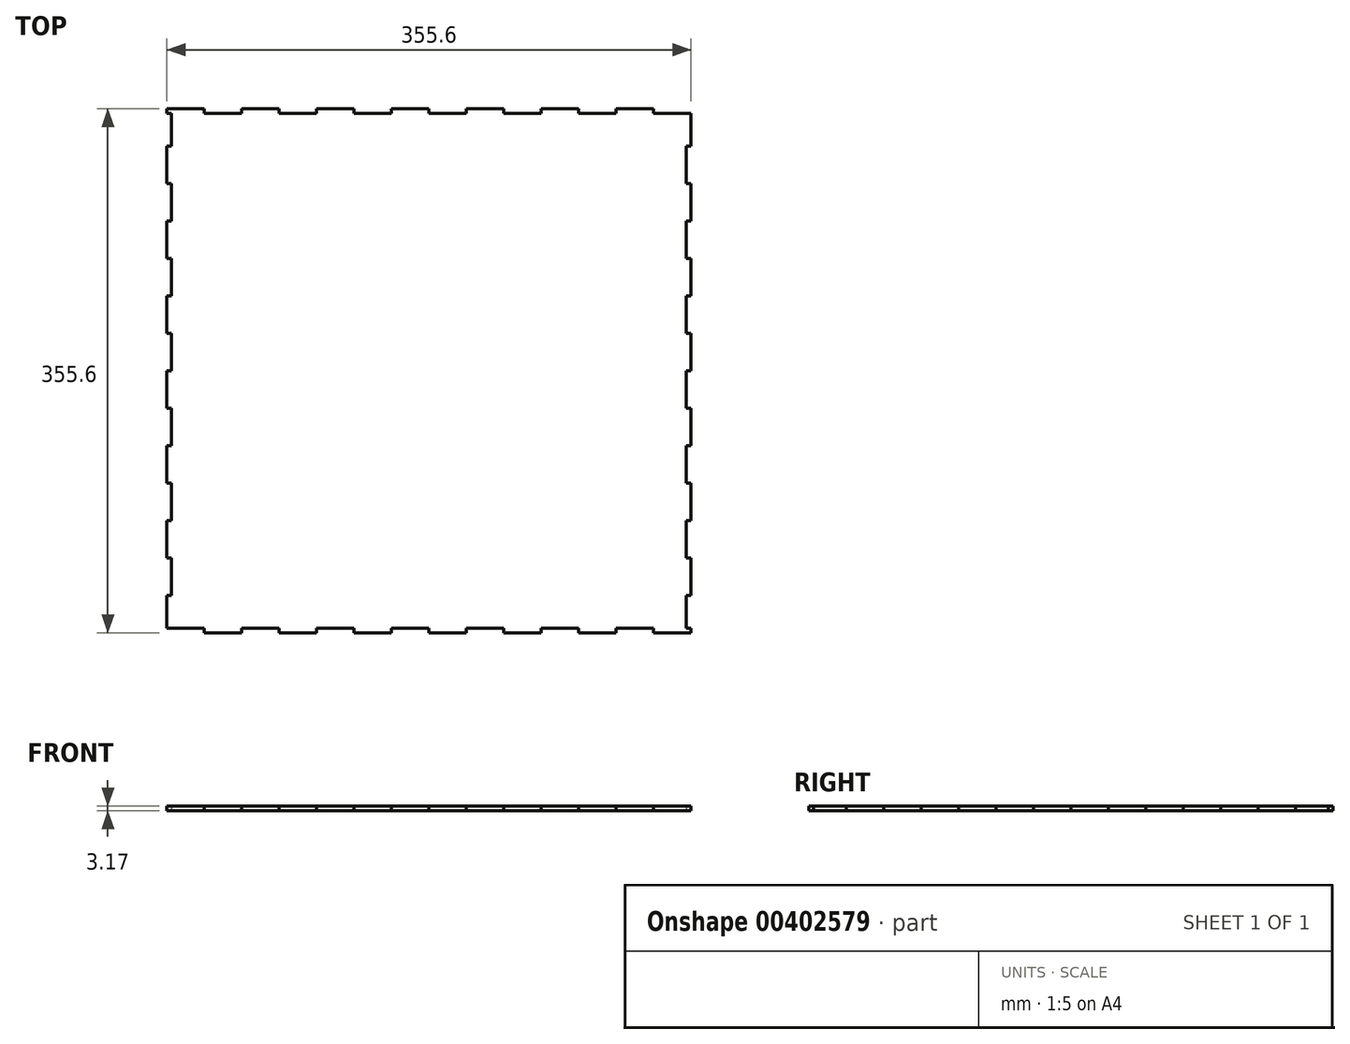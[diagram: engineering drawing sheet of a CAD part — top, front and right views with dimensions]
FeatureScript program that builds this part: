
annotation { "Feature Type Name" : "Feature", "Feature Type Description" : "" }
export const myFeature = defineFeature(function(context is Context, id is Id, definition is map)
    precondition{}
    {
        {
            var Q0;
            Q0=qCreatedBy(makeId("Top.planeOp"),FACE);
            var sketch = newSketch(context, id + "F0", { "sketchPlane" : qUnion([Q0])});
            skLineSegment(sketch, "E0.bottom", {"start": v(-177.8, 177.8) * mm, "end": v(-152.4, 177.8) * mm});
            skLineSegment(sketch, "E0.top", {"start": v(-152.4, -177.8) * mm, "end": v(-127, -177.8) * mm});
            skLineSegment(sketch, "E0.left", {"start": v(-177.8, 177.8) * mm, "end": v(-177.8, 174.62) * mm});
            skLineSegment(sketch, "E0.right", {"start": v(177.8, 174.62) * mm, "end": v(177.8, 152.4) * mm});
            skLineSegment(sketch, "E1", {"start": v(-174.62, 174.62) * mm, "end": v(-174.62, 152.4) * mm});
            skLineSegment(sketch, "E2", {"start": v(-152.4, 174.62) * mm, "end": v(-127, 174.62) * mm});
            skLineSegment(sketch, "E3", {"start": v(174.62, 152.4) * mm, "end": v(174.62, 127) * mm});
            skLineSegment(sketch, "E4", {"start": v(152.4, -174.62) * mm, "end": v(127, -174.62) * mm});
            skLineSegment(sketch, "E5", {"start": v(-152.4, 177.8) * mm, "end": v(-152.4, 174.62) * mm});
            skLineSegment(sketch, "E6", {"start": v(-174.62, 174.62) * mm, "end": v(-177.8, 174.62) * mm});
            skLineSegment(sketch, "E7", {"start": v(-127, 177.8) * mm, "end": v(-127, 174.62) * mm});
            skLineSegment(sketch, "E8", {"start": v(-101.6, 177.8) * mm, "end": v(-101.6, 174.62) * mm});
            skLineSegment(sketch, "E9", {"start": v(-76.2, 177.8) * mm, "end": v(-76.2, 174.62) * mm});
            skLineSegment(sketch, "E10", {"start": v(-50.8, 177.8) * mm, "end": v(-50.8, 174.62) * mm});
            skLineSegment(sketch, "E11", {"start": v(-25.4, 177.8) * mm, "end": v(-25.4, 174.62) * mm});
            skLineSegment(sketch, "E12", {"start": v(0, 177.8) * mm, "end": v(0, 174.62) * mm});
            skLineSegment(sketch, "E13", {"start": v(25.4, 177.8) * mm, "end": v(25.4, 174.62) * mm});
            skLineSegment(sketch, "E14", {"start": v(50.8, 177.8) * mm, "end": v(50.8, 174.62) * mm});
            skLineSegment(sketch, "E15", {"start": v(76.2, 177.8) * mm, "end": v(76.2, 174.63) * mm});
            skLineSegment(sketch, "E16", {"start": v(101.6, 177.8) * mm, "end": v(101.6, 174.63) * mm});
            skLineSegment(sketch, "E17", {"start": v(127, 177.8) * mm, "end": v(127, 174.63) * mm});
            skLineSegment(sketch, "E18", {"start": v(152.4, 177.8) * mm, "end": v(152.4, 174.63) * mm});
            skLineSegment(sketch, "E19.trimOffspring", {"start": v(-127, 177.8) * mm, "end": v(-101.6, 177.8) * mm});
            skLineSegment(sketch, "E20.trimOffspring", {"start": v(-101.6, 174.62) * mm, "end": v(-76.2, 174.62) * mm});
            skLineSegment(sketch, "E21.trimOffspring", {"start": v(-76.2, 177.8) * mm, "end": v(-50.8, 177.8) * mm});
            skLineSegment(sketch, "E22.trimOffspring", {"start": v(-50.8, 174.62) * mm, "end": v(-25.4, 174.62) * mm});
            skLineSegment(sketch, "E23.trimOffspring", {"start": v(-25.4, 177.8) * mm, "end": v(0, 177.8) * mm});
            skLineSegment(sketch, "E24.trimOffspring", {"start": v(0, 174.62) * mm, "end": v(25.4, 174.62) * mm});
            skLineSegment(sketch, "E25.trimOffspring", {"start": v(25.4, 177.8) * mm, "end": v(50.8, 177.8) * mm});
            skLineSegment(sketch, "E26.trimOffspring", {"start": v(50.8, 174.62) * mm, "end": v(76.2, 174.62) * mm});
            skLineSegment(sketch, "E27.trimOffspring", {"start": v(76.2, 177.8) * mm, "end": v(101.6, 177.8) * mm});
            skLineSegment(sketch, "E28.trimOffspring", {"start": v(101.6, 174.62) * mm, "end": v(127, 174.62) * mm});
            skLineSegment(sketch, "E29.trimOffspring", {"start": v(127, 177.8) * mm, "end": v(152.4, 177.8) * mm});
            skLineSegment(sketch, "E30.trimOffspring", {"start": v(152.4, 174.62) * mm, "end": v(174.63, 174.62) * mm});
            skLineSegment(sketch, "E31", {"start": v(174.62, 174.62) * mm, "end": v(177.8, 174.62) * mm});
            skLineSegment(sketch, "E32", {"start": v(-174.62, -174.62) * mm, "end": v(-177.8, -174.62) * mm});
            skLineSegment(sketch, "E33", {"start": v(152.4, -174.62) * mm, "end": v(152.4, -177.8) * mm});
            skLineSegment(sketch, "E34", {"start": v(127, -174.62) * mm, "end": v(127, -177.8) * mm});
            skLineSegment(sketch, "E35", {"start": v(101.6, -174.62) * mm, "end": v(101.6, -177.8) * mm});
            skLineSegment(sketch, "E36", {"start": v(76.2, -174.62) * mm, "end": v(76.2, -177.8) * mm});
            skLineSegment(sketch, "E37", {"start": v(50.8, -174.62) * mm, "end": v(50.8, -177.8) * mm});
            skLineSegment(sketch, "E38", {"start": v(25.4, -174.62) * mm, "end": v(25.4, -177.8) * mm});
            skPoint(sketch, "E39.endSnap0", {"position": v(0, -177.8) * mm});
            skLineSegment(sketch, "E40", {"start": v(-25.4, -174.62) * mm, "end": v(-25.4, -177.8) * mm});
            skLineSegment(sketch, "E41", {"start": v(-50.8, -174.62) * mm, "end": v(-50.8, -177.8) * mm});
            skLineSegment(sketch, "E42", {"start": v(-76.2, -174.62) * mm, "end": v(-76.2, -177.8) * mm});
            skLineSegment(sketch, "E43", {"start": v(-101.6, -174.62) * mm, "end": v(-101.6, -177.8) * mm});
            skLineSegment(sketch, "E44", {"start": v(-127, -174.62) * mm, "end": v(-127, -177.8) * mm});
            skLineSegment(sketch, "E45", {"start": v(-152.4, -174.62) * mm, "end": v(-152.4, -177.8) * mm});
            skPoint(sketch, "E46.orphan", {"position": v(-177.8, -177.8) * mm});
            skLineSegment(sketch, "E47.trimOffspring", {"start": v(-101.6, -177.8) * mm, "end": v(-76.2, -177.8) * mm});
            skLineSegment(sketch, "E48.trimOffspring", {"start": v(-101.6, -174.62) * mm, "end": v(-127, -174.62) * mm});
            skLineSegment(sketch, "E49.trimOffspring", {"start": v(-152.4, -174.62) * mm, "end": v(-174.62, -174.62) * mm});
            skLineSegment(sketch, "E50.trimOffspring", {"start": v(-50.8, -177.8) * mm, "end": v(-25.4, -177.8) * mm});
            skLineSegment(sketch, "E51.trimOffspring", {"start": v(-50.8, -174.62) * mm, "end": v(-76.2, -174.62) * mm});
            skLineSegment(sketch, "E52.trimOffspring", {"start": v(0, -177.8) * mm, "end": v(25.4, -177.8) * mm});
            skLineSegment(sketch, "E53", {"start": v(0, -174.62) * mm, "end": v(0, -177.8) * mm});
            skLineSegment(sketch, "E54.trimOffspring", {"start": v(0, -174.62) * mm, "end": v(-25.4, -174.62) * mm});
            skLineSegment(sketch, "E55.trimOffspring", {"start": v(50.8, -177.8) * mm, "end": v(76.2, -177.8) * mm});
            skLineSegment(sketch, "E56.trimOffspring", {"start": v(50.8, -174.62) * mm, "end": v(25.4, -174.62) * mm});
            skLineSegment(sketch, "E57.trimOffspring", {"start": v(101.6, -177.8) * mm, "end": v(127, -177.8) * mm});
            skLineSegment(sketch, "E58.trimOffspring", {"start": v(101.6, -174.62) * mm, "end": v(76.2, -174.62) * mm});
            skLineSegment(sketch, "E59.trimOffspring", {"start": v(152.4, -177.8) * mm, "end": v(177.8, -177.8) * mm});
            skLineSegment(sketch, "E60", {"start": v(174.62, -174.62) * mm, "end": v(177.8, -174.62) * mm});
            skLineSegment(sketch, "E61", {"start": v(174.62, 152.4) * mm, "end": v(177.8, 152.4) * mm});
            skLineSegment(sketch, "E62", {"start": v(174.62, 127) * mm, "end": v(177.8, 127) * mm});
            skLineSegment(sketch, "E63", {"start": v(174.62, 101.6) * mm, "end": v(177.8, 101.6) * mm});
            skLineSegment(sketch, "E64", {"start": v(174.62, 76.2) * mm, "end": v(177.8, 76.2) * mm});
            skLineSegment(sketch, "E65", {"start": v(174.62, 50.8) * mm, "end": v(177.8, 50.8) * mm});
            skLineSegment(sketch, "E66", {"start": v(174.62, 25.4) * mm, "end": v(177.8, 25.4) * mm});
            skLineSegment(sketch, "E67", {"start": v(174.62, 0) * mm, "end": v(177.8, 0) * mm});
            skLineSegment(sketch, "E68", {"start": v(174.62, -25.4) * mm, "end": v(177.8, -25.4) * mm});
            skLineSegment(sketch, "E69", {"start": v(174.62, -50.8) * mm, "end": v(177.8, -50.8) * mm});
            skLineSegment(sketch, "E70", {"start": v(174.62, -76.2) * mm, "end": v(177.8, -76.2) * mm});
            skLineSegment(sketch, "E71", {"start": v(174.62, -101.6) * mm, "end": v(177.8, -101.6) * mm});
            skLineSegment(sketch, "E72", {"start": v(174.62, -127) * mm, "end": v(177.8, -127) * mm});
            skLineSegment(sketch, "E73", {"start": v(174.62, -152.4) * mm, "end": v(177.8, -152.4) * mm});
            skLineSegment(sketch, "E74.trimOffspring", {"start": v(177.8, -174.62) * mm, "end": v(177.8, -177.8) * mm});
            skLineSegment(sketch, "E75.trimOffspring", {"start": v(174.62, -152.4) * mm, "end": v(174.62, -174.62) * mm});
            skLineSegment(sketch, "E76.trimOffspring", {"start": v(177.8, -127) * mm, "end": v(177.8, -152.4) * mm});
            skLineSegment(sketch, "E77.trimOffspring", {"start": v(174.62, -101.6) * mm, "end": v(174.62, -127) * mm});
            skLineSegment(sketch, "E78.trimOffspring", {"start": v(177.8, -76.2) * mm, "end": v(177.8, -101.6) * mm});
            skLineSegment(sketch, "E79.trimOffspring", {"start": v(174.62, -50.8) * mm, "end": v(174.62, -76.2) * mm});
            skLineSegment(sketch, "E80.trimOffspring", {"start": v(177.8, -25.4) * mm, "end": v(177.8, -50.8) * mm});
            skLineSegment(sketch, "E81.trimOffspring", {"start": v(174.62, 0) * mm, "end": v(174.62, -25.4) * mm});
            skLineSegment(sketch, "E82.trimOffspring", {"start": v(177.8, 25.4) * mm, "end": v(177.8, 0) * mm});
            skLineSegment(sketch, "E83.trimOffspring", {"start": v(174.62, 50.8) * mm, "end": v(174.62, 25.4) * mm});
            skLineSegment(sketch, "E84.trimOffspring", {"start": v(177.8, 76.2) * mm, "end": v(177.8, 50.8) * mm});
            skLineSegment(sketch, "E85.trimOffspring", {"start": v(174.62, 101.6) * mm, "end": v(174.62, 76.2) * mm});
            skLineSegment(sketch, "E86.trimOffspring", {"start": v(177.8, 127) * mm, "end": v(177.8, 101.6) * mm});
            skLineSegment(sketch, "E87", {"start": v(-177.8, 152.4) * mm, "end": v(-174.63, 152.4) * mm});
            skLineSegment(sketch, "E88", {"start": v(-177.8, 127) * mm, "end": v(-174.63, 127) * mm});
            skLineSegment(sketch, "E89", {"start": v(-177.8, 101.6) * mm, "end": v(-174.63, 101.6) * mm});
            skLineSegment(sketch, "E90", {"start": v(-177.8, 76.2) * mm, "end": v(-174.63, 76.2) * mm});
            skLineSegment(sketch, "E91", {"start": v(-177.8, 50.8) * mm, "end": v(-174.63, 50.8) * mm});
            skLineSegment(sketch, "E92", {"start": v(-177.8, 25.4) * mm, "end": v(-174.63, 25.4) * mm});
            skLineSegment(sketch, "E93", {"start": v(-177.8, 0) * mm, "end": v(-174.63, 0) * mm});
            skLineSegment(sketch, "E94", {"start": v(-177.8, -25.4) * mm, "end": v(-174.63, -25.4) * mm});
            skLineSegment(sketch, "E95", {"start": v(-177.8, -50.8) * mm, "end": v(-174.63, -50.8) * mm});
            skLineSegment(sketch, "E96", {"start": v(-177.8, -76.2) * mm, "end": v(-174.63, -76.2) * mm});
            skLineSegment(sketch, "E97", {"start": v(-177.8, -101.6) * mm, "end": v(-174.63, -101.6) * mm});
            skLineSegment(sketch, "E98", {"start": v(-177.8, -127) * mm, "end": v(-174.63, -127) * mm});
            skLineSegment(sketch, "E99", {"start": v(-177.8, -152.4) * mm, "end": v(-174.63, -152.4) * mm});
            skLineSegment(sketch, "E100.trimOffspring", {"start": v(-177.8, -152.4) * mm, "end": v(-177.8, -174.62) * mm});
            skLineSegment(sketch, "E101.trimOffspring", {"start": v(-174.62, -127) * mm, "end": v(-174.62, -152.4) * mm});
            skLineSegment(sketch, "E102.trimOffspring", {"start": v(-177.8, -101.6) * mm, "end": v(-177.8, -127) * mm});
            skLineSegment(sketch, "E103.trimOffspring", {"start": v(-174.62, -76.2) * mm, "end": v(-174.62, -101.6) * mm});
            skLineSegment(sketch, "E104.trimOffspring", {"start": v(-177.8, -50.8) * mm, "end": v(-177.8, -76.2) * mm});
            skLineSegment(sketch, "E105.trimOffspring", {"start": v(-174.62, -25.4) * mm, "end": v(-174.62, -50.8) * mm});
            skLineSegment(sketch, "E106.trimOffspring", {"start": v(-177.8, 0) * mm, "end": v(-177.8, -25.4) * mm});
            skLineSegment(sketch, "E107.trimOffspring", {"start": v(-174.62, 25.4) * mm, "end": v(-174.62, 0) * mm});
            skLineSegment(sketch, "E108.trimOffspring", {"start": v(-177.8, 50.8) * mm, "end": v(-177.8, 25.4) * mm});
            skLineSegment(sketch, "E109.trimOffspring", {"start": v(-174.62, 76.2) * mm, "end": v(-174.62, 50.8) * mm});
            skLineSegment(sketch, "E110.trimOffspring", {"start": v(-177.8, 101.6) * mm, "end": v(-177.8, 76.2) * mm});
            skLineSegment(sketch, "E111.trimOffspring", {"start": v(-174.62, 127) * mm, "end": v(-174.62, 101.6) * mm});
            skLineSegment(sketch, "E112.trimOffspring", {"start": v(-177.8, 152.4) * mm, "end": v(-177.8, 127) * mm});
            skSolve(sketch);
        }
        {
            var Q0;
            Q0 = qSketchRegion(id + "F0", true);
            extrude(context, id + "F1", {"entities" : qUnion([Q0]), "depth" : 3.17 * mm});
        }
    });
